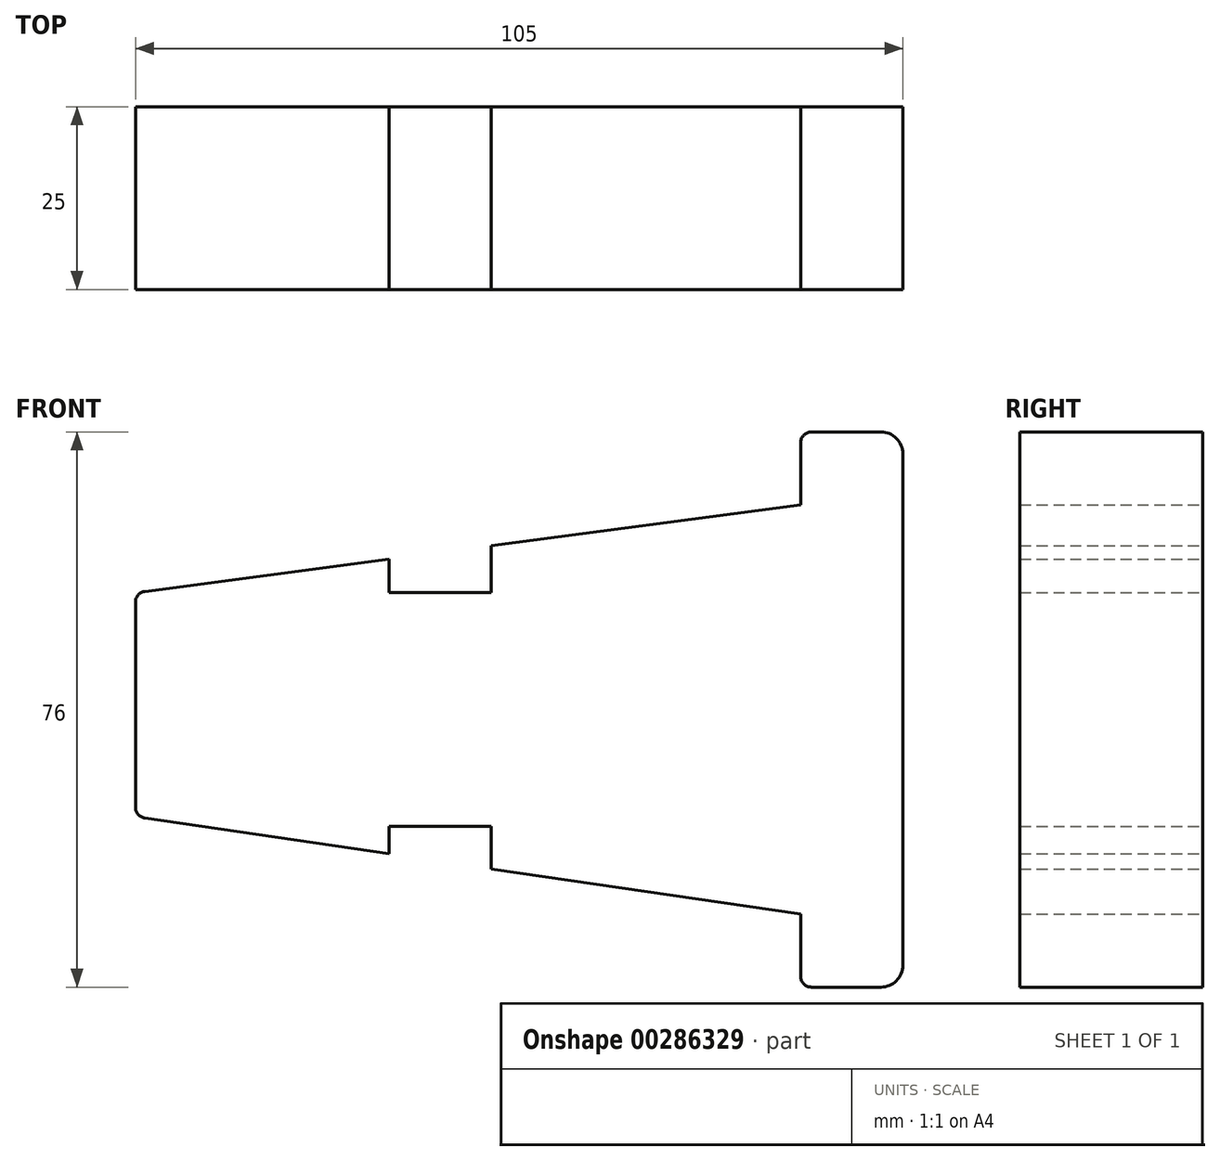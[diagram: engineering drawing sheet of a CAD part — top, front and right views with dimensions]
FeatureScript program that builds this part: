
annotation { "Feature Type Name" : "Feature", "Feature Type Description" : "" }
export const myFeature = defineFeature(function(context is Context, id is Id, definition is map)
    precondition{}
    {
        {
            var Q0;
            Q0=qCreatedBy(makeId("Front.planeOp"),FACE);
            var sketch = newSketch(context, id + "F0", { "sketchPlane" : qUnion([Q0])});
            skLineSegment(sketch, "E0", {"start": v(-42.3, -19.12) * mm, "end": v(-56.3, -19.12) * mm});
            skLineSegment(sketch, "E1", {"start": v(11, 34.88) * mm, "end": v(1.5, 34.88) * mm});
            skPoint(sketch, "E2.visualSharp", {"position": v(14, 34.88) * mm});
            skArc(sketch, "E2.filletArc", {"start": v(14, 31.88) * mm, "mid": v(13.12, 34) * mm, "end": v(11, 34.88) * mm});
            skLineSegment(sketch, "E3", {"start": v(0, 33.38) * mm, "end": v(0, 24.88) * mm});
            skPoint(sketch, "E4.visualSharp", {"position": v(0, 34.88) * mm});
            skArc(sketch, "E4.filletArc", {"start": v(1.5, 34.88) * mm, "mid": v(0.44, 34.44) * mm, "end": v(0, 33.38) * mm});
            skLineSegment(sketch, "E5", {"start": v(-91, -16.5) * mm, "end": v(-91, 11.56) * mm});
            skLineSegment(sketch, "E6", {"start": v(-89.7, 13.05) * mm, "end": v(-56.3, 17.45) * mm});
            skPoint(sketch, "E7.visualSharp", {"position": v(-91, 12.88) * mm});
            skArc(sketch, "E7.filletArc", {"start": v(-89.7, 13.05) * mm, "mid": v(-90.63, 12.55) * mm, "end": v(-91, 11.56) * mm});
            skPoint(sketch, "E8.visualSharp", {"position": v(-91, -19.12) * mm});
            skPoint(sketch, "E9.visualSharp", {"position": v(14, -19.12) * mm});
            skLineSegment(sketch, "E10", {"start": v(-91, 12.88) * mm, "end": v(-56.3, 17.45) * mm});
            skLineSegment(sketch, "E11", {"start": v(-56.3, 17.45) * mm, "end": v(-56.3, 12.88) * mm});
            skLineSegment(sketch, "E12", {"start": v(-56.3, 12.88) * mm, "end": v(-42.3, 12.88) * mm});
            skLineSegment(sketch, "E13", {"start": v(-42.3, 12.88) * mm, "end": v(-42.3, 19.3) * mm});
            skLineSegment(sketch, "E14.trimOffspring", {"start": v(-42.3, 19.3) * mm, "end": v(0, 24.88) * mm});
            skLineSegment(sketch, "E15", {"start": v(12.5, -19.12) * mm, "end": v(14, -19.12) * mm});
            skLineSegment(sketch, "E16", {"start": v(14, 34.88) * mm, "end": v(14, -38.12) * mm});
            skLineSegment(sketch, "E17", {"start": v(11, -41.12) * mm, "end": v(1.5, -41.12) * mm});
            skLineSegment(sketch, "E18", {"start": v(0, -39.62) * mm, "end": v(0, -31.12) * mm});
            skPoint(sketch, "E19.visualSharp", {"position": v(14, -41.12) * mm});
            skArc(sketch, "E19.filletArc", {"start": v(11, -41.12) * mm, "mid": v(13.12, -40.24) * mm, "end": v(14, -38.12) * mm});
            skPoint(sketch, "E20.visualSharp", {"position": v(0, -41.12) * mm});
            skArc(sketch, "E20.filletArc", {"start": v(0, -39.62) * mm, "mid": v(0.44, -40.68) * mm, "end": v(1.5, -41.12) * mm});
            skLineSegment(sketch, "E21", {"start": v(0, -31.12) * mm, "end": v(-42.3, -24.92) * mm});
            skLineSegment(sketch, "E22", {"start": v(-91, -17.62) * mm, "end": v(-91, -19.12) * mm});
            skLineSegment(sketch, "E23", {"start": v(-56.3, -19.12) * mm, "end": v(-56.3, -22.87) * mm});
            skLineSegment(sketch, "E24", {"start": v(-56.3, -22.87) * mm, "end": v(-56.3, -19.12) * mm});
            skLineSegment(sketch, "E25", {"start": v(-56.3, -19.12) * mm, "end": v(-42.3, -19.12) * mm});
            skLineSegment(sketch, "E26", {"start": v(-42.3, -19.12) * mm, "end": v(-42.3, -24.92) * mm});
            skLineSegment(sketch, "E27.trimOffspring", {"start": v(-56.3, -22.87) * mm, "end": v(-89.72, -17.98) * mm});
            skArc(sketch, "E28.filletArc", {"start": v(-91, -16.5) * mm, "mid": v(-90.63, -17.47) * mm, "end": v(-89.72, -17.98) * mm});
            skSolve(sketch);
        }
        {
            var Q0;
            Q0=makeQuery(id+"F0.imprint","IMPRINT",FACE,{"disambiguationData":[TD([[makeQuery(id+"F0.imprint","IMPRINT",EDGE,{"derivedFrom":sQuery(id+"F0.wireOp",EDGE,"E1")}),1.0]])]});
            extrude(context, id + "F1", {"entities" : qUnion([Q0]), "depth" : 25 * mm});
        }
    });
